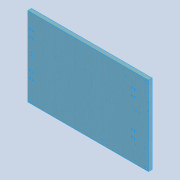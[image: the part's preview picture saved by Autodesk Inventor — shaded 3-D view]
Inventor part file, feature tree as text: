
AUTODESK INVENTOR PART (.ipt)
format: ipt  version: 2020 (Build 240168000, 168)  size: 333,824 bytes
history: native  units: mm
features: sketch x8, hole x6, other x4, extrude x3, reference x2, direct_edit x1, pattern_linear x1, projected_geometry x1, move_body x1
ambient origin geometry x8: Origin, YZ Plane, XZ Plane, XY Plane, X Axis, Y Axis, Z Axis, Center Point
bodies: Solid1 (feature_tree)
feature tree (27):
  extrude  "Extrusion1"  Depth=420.0mm
  extrude  "Extrusion2"  Depth=4.5mm
  extrude  "Extrusion3"  Depth=10.0mm
  direct_edit  "Direct Edit2"
  pattern_linear  "Rectangular Pattern1"  Count1=18  [1 undecoded]
  hole  "Hole1"  [1 undecoded]
  hole  "Hole2"  [1 undecoded]
  hole  "Hole3"  [1 undecoded]
  hole  "Hole4"  [1 undecoded]
  hole  "Hole5"  [1 undecoded]
  hole  "Hole6"  [1 undecoded]
  sketch  "Sketch1"  dims[d0=730.0mm d1=420.0mm]
  sketch  "Sketch2"  dims[d2=20.0mm d3=0.0mm d5=4.5mm]
  sketch  "Sketch3"  dims[d6=10.0mm d7=115.0mm d9=180.0mm]
  projected_geometry  "Projected Loop1"
  sketch  "Sketch5"  dims[d10=20.0mm d12=20.0mm d13=10.0mm d15=10.0mm d17=10.0mm d18=0.0mm]
  sketch  "Sketch6"  dims[d23=35.0mm d24=16.0mm]
  sketch  "Sketch7"  dims[d25=5.0mm d26=4.5mm]
  reference  "Reference3"
  reference  "Reference4"
  sketch  "Sketch8"  dims[d29=115.0mm d30=73.773mm]
  sketch  "Sketch9"  dims[d33=10.0mm d34=0.0mm d35=20.0mm d37=190.0mm d38=20.0mm d40=538.034mm d43=8.0mm d44=6.0mm d45=4.0mm d46=2.0mm d47=90.0deg d48=8.0mm d49=20.594885mm d53=0.0mm d54=0.0mm d55=-90.0mm d56=10.0mm d57=10.0mm d58=10.0mm d59=10.0mm d60=4.0mm d61=6.0mm d62=4.0mm d63=2.0mm d64=90.0deg d65=8.0mm d66=20.594885mm d67=20.0mm d68=20.0mm d69=8.0mm d70=6.0mm d71=4.0mm d72=2.0mm d73=90.0deg d74=8.0mm d75=20.594885mm d76=241.1mm d77=245.0mm d78=38.91mm d79=50.0mm d80=12.5mm d81=12.5mm d82=51.5mm d83=4.5mm d84=10.0mm d85=4.0mm d86=2.0mm d87=90.0deg d88=8.0mm d89=20.594885mm d90=2.459mm d91=20.0mm d92=4.0mm d93=2.0mm d94=90.0deg d95=8.0mm d96=20.594885mm d97=4.0mm d98=20.0mm d99=4.0mm d100=2.0mm d101=90.0deg d102=8.0mm d103=20.594885mm]
  move_body  "Move2"
  parser-record x1  (decoder bookkeeping rows leaked as tree rows — omitted from the tree; the rows remain in map.json)
  other  "0005-10-03 Y axis.iam"
  other  "0005-10-020 suport motor y.ipt:13"
  other  "0005-10-1001 NEMA17 - Motor de passo.ipt:8"
note: 7 required parameter values undecoded (feature->parameter linkage not recoverable at this tier; creation-order binding heuristic only, values carry confidence <= 0.55)
note: 1 file-system path scrubbed to <path> (originals preserved in map.json)
